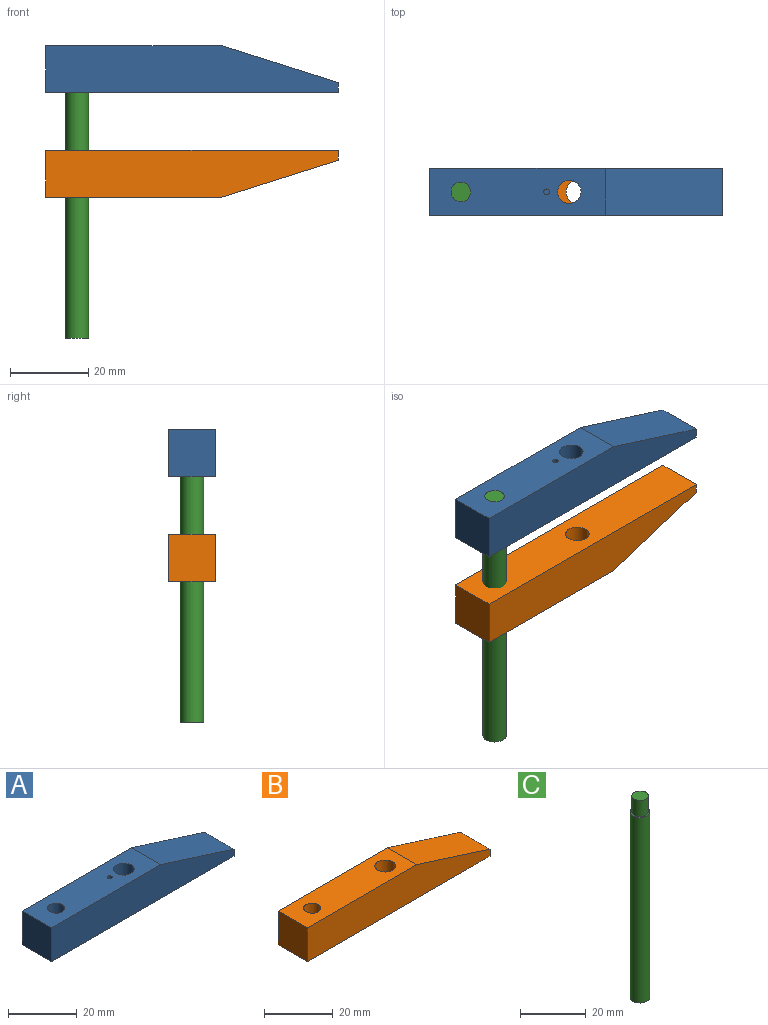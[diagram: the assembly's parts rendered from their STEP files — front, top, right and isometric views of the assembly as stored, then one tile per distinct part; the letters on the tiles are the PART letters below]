
ASSEMBLY  parts=3 mates=2
PART A: 11 faces, bbox 75x12x12 mm
  f0: plane 45x12mm, normal (0,0,1), area 490.3mm2, adj f1,f4,f5,f6,f7,f8,f10
  f1: plane 12x12mm, normal (-1,0,0), area 144mm2, adj f0,f2,f5,f6
  f2: plane 75x12mm, normal (0,0,-1), area 852.1mm2, adj f1,f3,f5,f6,f7,f10
  f3: plane 12x2.5mm, normal (1,0,0), area 30mm2, adj f2,f4,f5,f6
  f4: plane 30x12mm, normal (0.3,0,0.95), area 377.6mm2, adj f0,f3,f5,f6
  f5: plane 75x12mm, normal (0,1,0), area 757.5mm2, adj f0,f1,f2,f3,f4
  f6: plane 75x12mm, normal (0,-1,0), area 757.5mm2, adj f0,f1,f2,f3,f4
  f7: cylinder r=3mm len=12mm, axis (0,0,1), area 226.2mm2, adj f0,f2
  f8: cylinder r=0.75mm len=5mm, axis (0,0,1), area 23.6mm2, adj f0,f9
  f9: plane 1.5x1.5mm, normal (0,0,1), area 1.8mm2, adj f8
  f10: cylinder r=2.5mm len=12mm, axis (0,0,-1), area 188.5mm2, adj f0,f2
PART B: 9 faces, bbox 75x12x12 mm
  f0: plane 30x12mm, normal (0.3,0,0.95), area 377.6mm2, adj f1,f4,f5,f6
  f1: plane 45x12mm, normal (0,0,1), area 492.1mm2, adj f0,f2,f5,f6,f7,f8
  f2: plane 12x12mm, normal (-1,0,0), area 144mm2, adj f1,f3,f5,f6
  f3: plane 75x12mm, normal (0,0,-1), area 852.1mm2, adj f2,f4,f5,f6,f7,f8
  f4: plane 12x2.5mm, normal (1,0,0), area 30mm2, adj f0,f3,f5,f6
  f5: plane 75x12mm, normal (0,-1,0), area 757.5mm2, adj f0,f1,f2,f3,f4
  f6: plane 75x12mm, normal (0,1,0), area 757.5mm2, adj f0,f1,f2,f3,f4
  f7: cylinder r=2.5mm len=12mm, axis (0,0,1), area 188.5mm2, adj f1,f3
  f8: cylinder r=3mm len=12mm, axis (0,0,1), area 226.2mm2, adj f1,f3
PART C: 5 faces, bbox 6x6x75 mm
  f0: cylinder r=2.5mm len=6mm, axis (0,0,-1), area 94.2mm2, adj f1,f4
  f1: plane 5x5mm, normal (0,0,1), area 19.6mm2, adj f0
  f2: cylinder r=3mm len=69mm, axis (0,0,1), area 1300.6mm2, adj f3,f4
  f3: plane 6x6mm, normal (0,0,-1), area 28.3mm2, adj f2
  f4: plane 6x6mm, normal (0,0,1), area 8.6mm2, adj f0,f2
PLACE A t=(5.84,3.9,-4.02)mm
PLACE B rot(axis=(1,0,0),180deg) t=(10.8,3.9,-7.12)mm
PLACE C t=(-21.96,9.9,11.2)mm
MATE fastened C.f0 <-> A.f10  axis (0,0,1) through (-21.96,9.9,17.2)mm
MATE slider B.f7 <-> C.f0  axis (0,0,-1) through (-21.96,9.9,-21.65)mm
